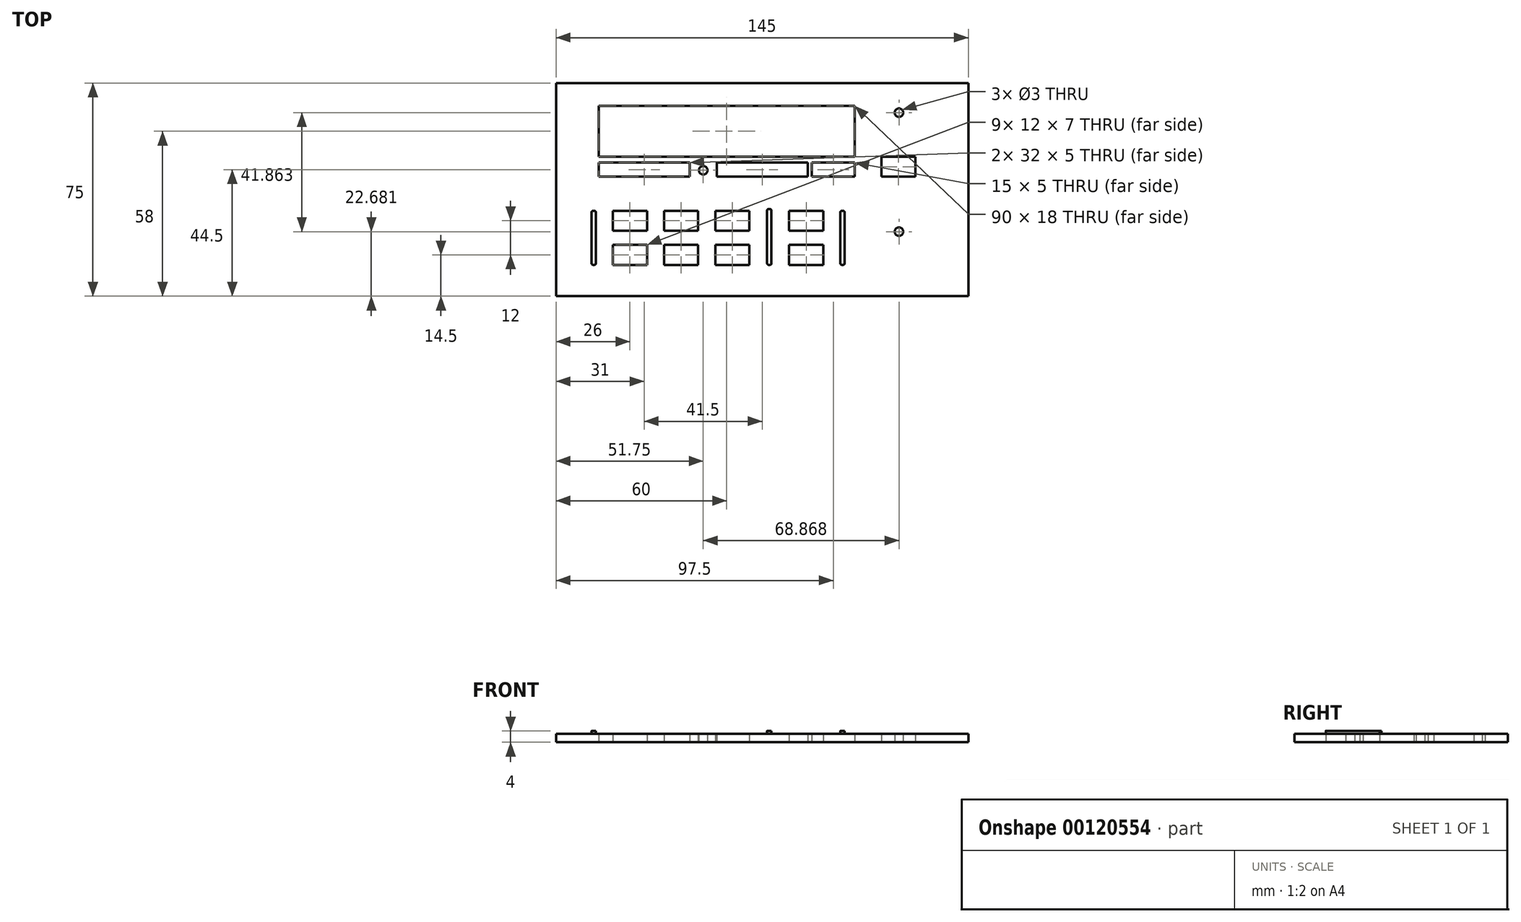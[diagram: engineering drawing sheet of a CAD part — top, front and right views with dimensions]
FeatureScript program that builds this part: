
annotation { "Feature Type Name" : "Feature", "Feature Type Description" : "" }
export const myFeature = defineFeature(function(context is Context, id is Id, definition is map)
    precondition{}
    {
        {
            var Q0;
            Q0=qCreatedBy(makeId("Top.planeOp"),FACE);
            var sketch = newSketch(context, id + "F0", { "sketchPlane" : qUnion([Q0])});
            skLineSegment(sketch, "E0.bottom", {"start": v(0, 0) * mm, "end": v(145, 0) * mm});
            skLineSegment(sketch, "E0.left", {"start": v(0, 0) * mm, "end": v(0, -75) * mm});
            skLineSegment(sketch, "E0.right", {"start": v(145, 0) * mm, "end": v(145, -75) * mm});
            skLineSegment(sketch, "E1.bottom", {"start": v(15, -8) * mm, "end": v(105, -8) * mm});
            skLineSegment(sketch, "E1.top", {"start": v(15, -26) * mm, "end": v(105, -26) * mm});
            skLineSegment(sketch, "E1.left", {"start": v(15, -8) * mm, "end": v(15, -26) * mm});
            skLineSegment(sketch, "E1.right", {"start": v(105, -8) * mm, "end": v(105, -26) * mm});
            skCircle(sketch, "E2", {"center": v(120.62, -10.46) * mm, "radius": 7 * mm, "construction": true});
            skCircle(sketch, "E3", {"center": v(120.62, -10.46) * mm, "radius": 1.5 * mm});
            skCircle(sketch, "E4", {"center": v(120.62, -52.32) * mm, "radius": 8.5 * mm, "construction": true});
            skCircle(sketch, "E5", {"center": v(120.62, -52.32) * mm, "radius": 1.5 * mm});
            skLineSegment(sketch, "E6.bottom", {"start": v(114.43, -26) * mm, "end": v(126.43, -26) * mm});
            skLineSegment(sketch, "E6.top", {"start": v(114.43, -33) * mm, "end": v(126.43, -33) * mm});
            skLineSegment(sketch, "E6.left", {"start": v(114.43, -26) * mm, "end": v(114.43, -33) * mm});
            skLineSegment(sketch, "E6.right", {"start": v(126.43, -26) * mm, "end": v(126.43, -33) * mm});
            skLineSegment(sketch, "E7.bottom", {"start": v(15, -28) * mm, "end": v(47, -28) * mm});
            skLineSegment(sketch, "E7.top", {"start": v(15, -33) * mm, "end": v(47, -33) * mm});
            skLineSegment(sketch, "E7.left", {"start": v(15, -28) * mm, "end": v(15, -33) * mm});
            skLineSegment(sketch, "E7.right", {"start": v(47, -28) * mm, "end": v(47, -33) * mm});
            skLineSegment(sketch, "E8.bottom", {"start": v(56.5, -28) * mm, "end": v(88.5, -28) * mm});
            skLineSegment(sketch, "E8.top", {"start": v(56.5, -33) * mm, "end": v(88.5, -33) * mm});
            skLineSegment(sketch, "E8.left", {"start": v(56.5, -28) * mm, "end": v(56.5, -33) * mm});
            skLineSegment(sketch, "E8.right", {"start": v(88.5, -28) * mm, "end": v(88.5, -33) * mm});
            skLineSegment(sketch, "E9.bottom", {"start": v(105, -28) * mm, "end": v(90, -28) * mm});
            skLineSegment(sketch, "E9.top", {"start": v(105, -33) * mm, "end": v(90, -33) * mm});
            skLineSegment(sketch, "E9.left", {"start": v(105, -28) * mm, "end": v(105, -33) * mm});
            skLineSegment(sketch, "E9.right", {"start": v(90, -28) * mm, "end": v(90, -33) * mm});
            skCircle(sketch, "E10", {"center": v(51.75, -30.72) * mm, "radius": 1.5 * mm});
            skLineSegment(sketch, "E11.bottom", {"start": v(38, -45) * mm, "end": v(50, -45) * mm});
            skLineSegment(sketch, "E11.top", {"start": v(38, -52) * mm, "end": v(50, -52) * mm});
            skLineSegment(sketch, "E11.left", {"start": v(38, -45) * mm, "end": v(38, -52) * mm});
            skLineSegment(sketch, "E11.right", {"start": v(50, -45) * mm, "end": v(50, -52) * mm});
            skLineSegment(sketch, "E12.bottom", {"start": v(56, -45) * mm, "end": v(68, -45) * mm});
            skLineSegment(sketch, "E12.top", {"start": v(56, -52) * mm, "end": v(68, -52) * mm});
            skLineSegment(sketch, "E12.left", {"start": v(56, -45) * mm, "end": v(56, -52) * mm});
            skLineSegment(sketch, "E12.right", {"start": v(68, -45) * mm, "end": v(68, -52) * mm});
            skLineSegment(sketch, "E13.bottom", {"start": v(20, -45) * mm, "end": v(32, -45) * mm});
            skLineSegment(sketch, "E13.top", {"start": v(20, -52) * mm, "end": v(32, -52) * mm});
            skLineSegment(sketch, "E13.left", {"start": v(20, -45) * mm, "end": v(20, -52) * mm});
            skLineSegment(sketch, "E13.right", {"start": v(32, -45) * mm, "end": v(32, -52) * mm});
            skLineSegment(sketch, "E14.bottom", {"start": v(20, -57) * mm, "end": v(32, -57) * mm});
            skLineSegment(sketch, "E14.top", {"start": v(20, -64) * mm, "end": v(32, -64) * mm});
            skLineSegment(sketch, "E14.left", {"start": v(20, -57) * mm, "end": v(20, -64) * mm});
            skLineSegment(sketch, "E14.right", {"start": v(32, -57) * mm, "end": v(32, -64) * mm});
            skLineSegment(sketch, "E15.bottom", {"start": v(38, -57) * mm, "end": v(50, -57) * mm});
            skLineSegment(sketch, "E15.top", {"start": v(38, -64) * mm, "end": v(50, -64) * mm});
            skLineSegment(sketch, "E15.left", {"start": v(38, -57) * mm, "end": v(38, -64) * mm});
            skLineSegment(sketch, "E15.right", {"start": v(50, -57) * mm, "end": v(50, -64) * mm});
            skLineSegment(sketch, "E16", {"start": v(0, -75) * mm, "end": v(145, -75) * mm});
            skLineSegment(sketch, "E17", {"start": v(56, -57) * mm, "end": v(56, -64) * mm});
            skLineSegment(sketch, "E18", {"start": v(56, -64) * mm, "end": v(68, -64) * mm});
            skLineSegment(sketch, "E19", {"start": v(68, -64) * mm, "end": v(68, -57) * mm});
            skLineSegment(sketch, "E20", {"start": v(68, -57) * mm, "end": v(56, -57) * mm});
            skLineSegment(sketch, "E21.bottom", {"start": v(82, -57) * mm, "end": v(94, -57) * mm});
            skLineSegment(sketch, "E21.top", {"start": v(82, -64) * mm, "end": v(94, -64) * mm});
            skLineSegment(sketch, "E21.left", {"start": v(82, -57) * mm, "end": v(82, -64) * mm});
            skLineSegment(sketch, "E21.right", {"start": v(94, -57) * mm, "end": v(94, -64) * mm});
            skLineSegment(sketch, "E22.bottom", {"start": v(82, -45) * mm, "end": v(94, -45) * mm});
            skLineSegment(sketch, "E22.top", {"start": v(82, -52) * mm, "end": v(94, -52) * mm});
            skLineSegment(sketch, "E22.left", {"start": v(82, -45) * mm, "end": v(82, -52) * mm});
            skLineSegment(sketch, "E22.right", {"start": v(94, -45) * mm, "end": v(94, -52) * mm});
            skSolve(sketch);
        }
        {
            var Q0;
            Q0=makeQuery(id+"F0.imprint","IMPRINT",FACE,{"disambiguationData":[TD([[makeQuery(id+"F0.imprint","IMPRINT",EDGE,{"derivedFrom":sQuery(id+"F0.wireOp",EDGE,"E0.bottom")}),-1.0]])]});
            extrude(context, id + "F1", {"entities" : qUnion([Q0]), "depth" : 3 * mm});
        }
        {
            var Q0;
            Q0=makeQuery(id+"F1.opExtrude","CAP_FACE",FACE,{"disambiguationData":[OSD([sQuery(id+"F0.wireOp",EDGE,"E0.bottom"),sQuery(id+"F0.wireOp",EDGE,"E0.left"),sQuery(id+"F0.wireOp",EDGE,"E0.right"),sQuery(id+"F0.wireOp",EDGE,"E1.bottom"),sQuery(id+"F0.wireOp",EDGE,"E1.top"),sQuery(id+"F0.wireOp",EDGE,"E1.left"),sQuery(id+"F0.wireOp",EDGE,"E1.right"),sQuery(id+"F0.wireOp",EDGE,"E3"),sQuery(id+"F0.wireOp",EDGE,"E5"),sQuery(id+"F0.wireOp",EDGE,"E6.bottom"),sQuery(id+"F0.wireOp",EDGE,"E6.top"),sQuery(id+"F0.wireOp",EDGE,"E6.left"),sQuery(id+"F0.wireOp",EDGE,"E6.right"),sQuery(id+"F0.wireOp",EDGE,"E7.bottom"),sQuery(id+"F0.wireOp",EDGE,"E7.top"),sQuery(id+"F0.wireOp",EDGE,"E7.left"),sQuery(id+"F0.wireOp",EDGE,"E7.right"),sQuery(id+"F0.wireOp",EDGE,"E8.bottom"),sQuery(id+"F0.wireOp",EDGE,"E8.top"),sQuery(id+"F0.wireOp",EDGE,"E8.left"),sQuery(id+"F0.wireOp",EDGE,"E8.right"),sQuery(id+"F0.wireOp",EDGE,"E9.bottom"),sQuery(id+"F0.wireOp",EDGE,"E9.top"),sQuery(id+"F0.wireOp",EDGE,"E9.left"),sQuery(id+"F0.wireOp",EDGE,"E9.right"),sQuery(id+"F0.wireOp",EDGE,"E10"),sQuery(id+"F0.wireOp",EDGE,"E11.bottom"),sQuery(id+"F0.wireOp",EDGE,"E11.top"),sQuery(id+"F0.wireOp",EDGE,"E11.left"),sQuery(id+"F0.wireOp",EDGE,"E11.right"),sQuery(id+"F0.wireOp",EDGE,"E12.bottom"),sQuery(id+"F0.wireOp",EDGE,"E12.top"),sQuery(id+"F0.wireOp",EDGE,"E12.left"),sQuery(id+"F0.wireOp",EDGE,"E12.right"),sQuery(id+"F0.wireOp",EDGE,"E13.bottom"),sQuery(id+"F0.wireOp",EDGE,"E13.top"),sQuery(id+"F0.wireOp",EDGE,"E13.left"),sQuery(id+"F0.wireOp",EDGE,"E13.right"),sQuery(id+"F0.wireOp",EDGE,"E14.bottom"),sQuery(id+"F0.wireOp",EDGE,"E14.top"),sQuery(id+"F0.wireOp",EDGE,"E14.left"),sQuery(id+"F0.wireOp",EDGE,"E14.right"),sQuery(id+"F0.wireOp",EDGE,"E15.bottom"),sQuery(id+"F0.wireOp",EDGE,"E15.top"),sQuery(id+"F0.wireOp",EDGE,"E15.left"),sQuery(id+"F0.wireOp",EDGE,"E15.right"),sQuery(id+"F0.wireOp",EDGE,"E16"),sQuery(id+"F0.wireOp",EDGE,"E17"),sQuery(id+"F0.wireOp",EDGE,"E18"),sQuery(id+"F0.wireOp",EDGE,"E19"),sQuery(id+"F0.wireOp",EDGE,"E20"),sQuery(id+"F0.wireOp",EDGE,"E21.bottom"),sQuery(id+"F0.wireOp",EDGE,"E21.top"),sQuery(id+"F0.wireOp",EDGE,"E21.left"),sQuery(id+"F0.wireOp",EDGE,"E21.right"),sQuery(id+"F0.wireOp",EDGE,"E22.bottom"),sQuery(id+"F0.wireOp",EDGE,"E22.top"),sQuery(id+"F0.wireOp",EDGE,"E22.left"),sQuery(id+"F0.wireOp",EDGE,"E22.right")])],"isStart":false});
            var sketch = newSketch(context, id + "F2", { "sketchPlane" : qUnion([Q0])});
            skLineSegment(sketch, "E23.bottom", {"start": v(13, -45) * mm, "end": v(13.5, -45) * mm});
            skLineSegment(sketch, "E23.top", {"start": v(13, -64) * mm, "end": v(13.5, -64) * mm});
            skLineSegment(sketch, "E23.left", {"start": v(12.5, -45.5) * mm, "end": v(12.5, -63.5) * mm});
            skLineSegment(sketch, "E23.right", {"start": v(14, -45.5) * mm, "end": v(14, -63.5) * mm});
            skLineSegment(sketch, "E24.bottom", {"start": v(100.5, -45) * mm, "end": v(101, -45) * mm});
            skLineSegment(sketch, "E24.top", {"start": v(100.5, -64) * mm, "end": v(101, -64) * mm});
            skLineSegment(sketch, "E24.left", {"start": v(101.5, -45.5) * mm, "end": v(101.5, -63.5) * mm});
            skLineSegment(sketch, "E24.right", {"start": v(100, -45.5) * mm, "end": v(100, -63.5) * mm});
            skLineSegment(sketch, "E25.bottom", {"start": v(74.75, -44.36) * mm, "end": v(75.25, -44.36) * mm});
            skLineSegment(sketch, "E25.top", {"start": v(74.75, -64) * mm, "end": v(75.25, -64) * mm});
            skLineSegment(sketch, "E25.left", {"start": v(74.25, -44.86) * mm, "end": v(74.25, -63.5) * mm});
            skLineSegment(sketch, "E25.right", {"start": v(75.75, -44.86) * mm, "end": v(75.75, -63.5) * mm});
            skPoint(sketch, "E26.visualSharp", {"position": v(12.5, -45) * mm});
            skArc(sketch, "E26.filletArc", {"start": v(13, -45) * mm, "mid": v(12.65, -45.15) * mm, "end": v(12.5, -45.5) * mm});
            skPoint(sketch, "E27.visualSharp", {"position": v(14, -45) * mm});
            skArc(sketch, "E27.filletArc", {"start": v(14, -45.5) * mm, "mid": v(13.85, -45.15) * mm, "end": v(13.5, -45) * mm});
            skPoint(sketch, "E28.visualSharp", {"position": v(12.5, -64) * mm});
            skArc(sketch, "E28.filletArc", {"start": v(12.5, -63.5) * mm, "mid": v(12.65, -63.85) * mm, "end": v(13, -64) * mm});
            skPoint(sketch, "E29.visualSharp", {"position": v(14, -64) * mm});
            skArc(sketch, "E29.filletArc", {"start": v(13.5, -64) * mm, "mid": v(13.85, -63.85) * mm, "end": v(14, -63.5) * mm});
            skPoint(sketch, "E30.visualSharp", {"position": v(74.25, -44.36) * mm});
            skArc(sketch, "E30.filletArc", {"start": v(74.75, -44.36) * mm, "mid": v(74.4, -44.51) * mm, "end": v(74.25, -44.86) * mm});
            skPoint(sketch, "E31.visualSharp", {"position": v(75.75, -44.36) * mm});
            skArc(sketch, "E31.filletArc", {"start": v(75.75, -44.86) * mm, "mid": v(75.6, -44.51) * mm, "end": v(75.25, -44.36) * mm});
            skPoint(sketch, "E32.visualSharp", {"position": v(74.25, -64) * mm});
            skArc(sketch, "E32.filletArc", {"start": v(74.25, -63.5) * mm, "mid": v(74.4, -63.85) * mm, "end": v(74.75, -64) * mm});
            skPoint(sketch, "E33.visualSharp", {"position": v(75.75, -64) * mm});
            skArc(sketch, "E33.filletArc", {"start": v(75.25, -64) * mm, "mid": v(75.6, -63.85) * mm, "end": v(75.75, -63.5) * mm});
            skPoint(sketch, "E34.visualSharp", {"position": v(100, -45) * mm});
            skArc(sketch, "E34.filletArc", {"start": v(100.5, -45) * mm, "mid": v(100.15, -45.15) * mm, "end": v(100, -45.5) * mm});
            skPoint(sketch, "E35.visualSharp", {"position": v(101.5, -45) * mm});
            skArc(sketch, "E35.filletArc", {"start": v(101.5, -45.5) * mm, "mid": v(101.35, -45.15) * mm, "end": v(101, -45) * mm});
            skPoint(sketch, "E36.visualSharp", {"position": v(100, -64) * mm});
            skArc(sketch, "E36.filletArc", {"start": v(100, -63.5) * mm, "mid": v(100.15, -63.85) * mm, "end": v(100.5, -64) * mm});
            skPoint(sketch, "E37.visualSharp", {"position": v(101.5, -64) * mm});
            skArc(sketch, "E37.filletArc", {"start": v(101, -64) * mm, "mid": v(101.35, -63.85) * mm, "end": v(101.5, -63.5) * mm});
            skSolve(sketch);
        }
        {
            var Q0;
            Q0 = qSketchRegion(id + "F2", true);
            extrude(context, id + "F3", {"entities" : qUnion([Q0]), "operationType" : NewBodyOperationType.ADD, "depth" : 1 * mm});
        }
    });
